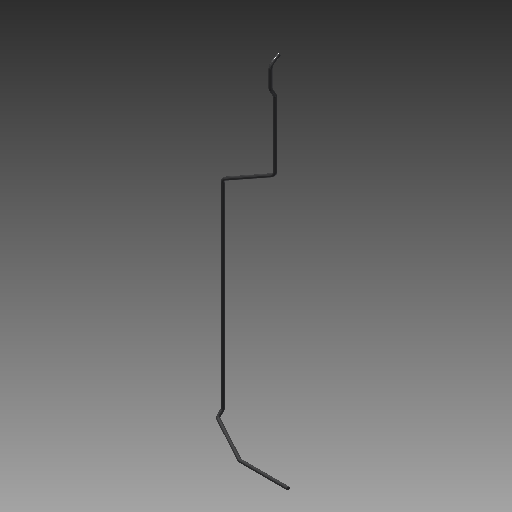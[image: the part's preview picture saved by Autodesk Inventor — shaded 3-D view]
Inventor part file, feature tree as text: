
AUTODESK INVENTOR PART (.ipt)
format: ipt  version: 2019 (Build 230136000, 136)  size: 99,328 bytes
history: native  units: mm
features: other x3, plane x2
ambient origin geometry x8: Origin, YZ Plane, XZ Plane, XY Plane, X Axis, Y Axis, Z Axis, Center Point
bodies: Solid1 (feature_tree)
feature tree (5):
  other  "Tension Cage R.ipt"
  other  "Work Axis1"
  plane  "Work Plane1"
  plane  "Work Plane2"
  other  "Solid1::Tension Cage R.ipt"
